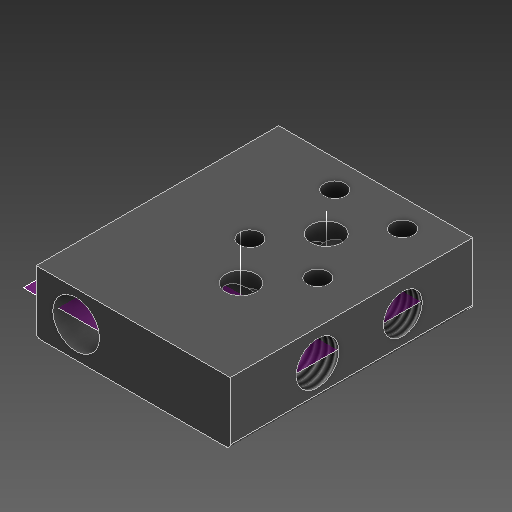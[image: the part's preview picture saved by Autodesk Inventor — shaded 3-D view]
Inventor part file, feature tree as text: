
AUTODESK INVENTOR PART (.ipt)
format: ipt  version: 2021 (Build 250183000, 183)  size: 229,888 bytes
history: native  units: in
note: dims shown in document units (in); Inventor stores cm internally (conversion verified against a paired STEP export)
features: other x6, sketch x4, plane x3
ambient origin geometry x8: Origin, YZ Plane, XZ Plane, XY Plane, X Axis, Y Axis, Z Axis, Center Point
bodies: Solid1 (feature_tree)
feature tree (13):
  other  "Val_BodV4.ipt"
  other  "Solid1::Val_BodV4.ipt"
  other  "TaggingFeature1"
  sketch  "Sketch3"  dims[d0=0.3937in]
  sketch  "Sketch5"
  sketch  "Sketch6"
  sketch  "Sketch4"
  plane  "Work Plane1"
  plane  "Work Plane2"
  plane  "Work Plane3"
  other  "Work Axis1"
  other  "Work Axis2"
  other  "Work Axis3"
